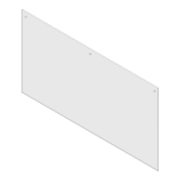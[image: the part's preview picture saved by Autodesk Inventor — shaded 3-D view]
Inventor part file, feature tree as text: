
AUTODESK INVENTOR PART (.ipt)
format: ipt  version: 2012 (Build 160160000, 160)  size: 76,288 bytes
history: native  units: in
note: dims shown in document units (in); Inventor stores cm internally (conversion verified against a paired STEP export)
features: extrude x1, sketch x1
ambient origin geometry x8: Origin, YZ Plane, XZ Plane, XY Plane, X Axis, Y Axis, Z Axis, Center Point
bodies: Solid1 (feature_tree)
feature tree (2):
  extrude  "Extrusion1"  Depth=19.0in
  sketch  "Sketch1"  dims[d0=36.0in d1=19.0in d2=0.375in d3=0.375in d4=0.375in d5=1.25in d6=1.25in d7=1.25in d8=1.0in d9=18.0in d10=35.0in d11=0.25in d12=0.0in]
